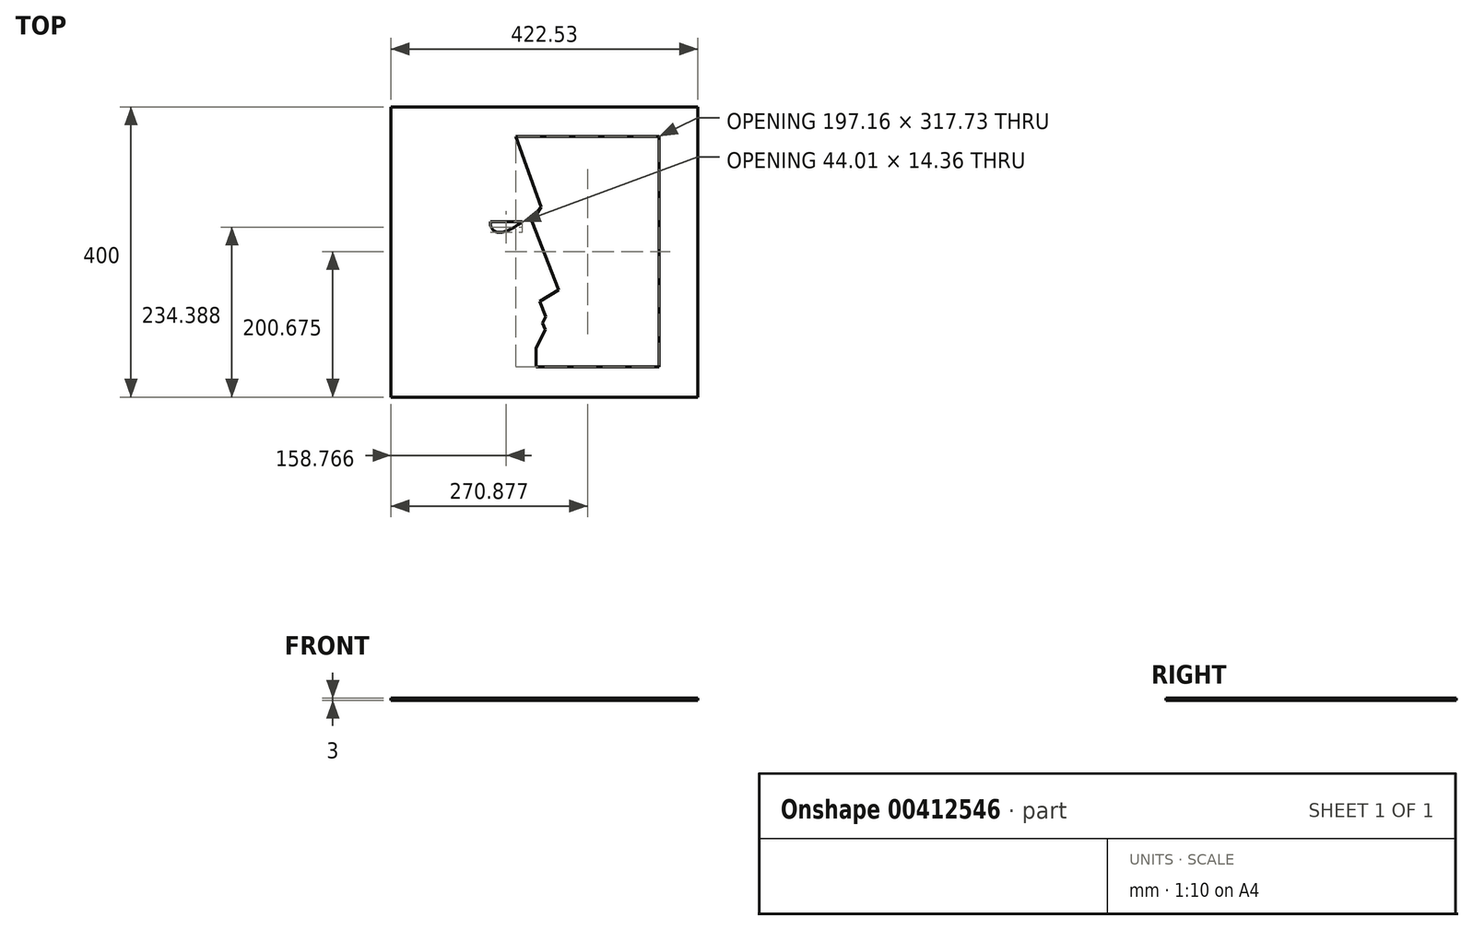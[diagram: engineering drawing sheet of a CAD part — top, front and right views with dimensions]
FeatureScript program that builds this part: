
annotation { "Feature Type Name" : "Feature", "Feature Type Description" : "" }
export const myFeature = defineFeature(function(context is Context, id is Id, definition is map)
    precondition{}
    {
        {
            var Q0;
            Q0=qCreatedBy(makeId("Top.planeOp"),FACE);
            var sketch = newSketch(context, id + "F0", { "sketchPlane" : qUnion([Q0])});
            skLineSegment(sketch, "E0", {"start": v(35.06, -8.57) * mm, "end": v(457.6, -8.57) * mm});
            skLineSegment(sketch, "E1", {"start": v(457.6, -408.57) * mm, "end": v(35.06, -408.57) * mm});
            skLineSegment(sketch, "E2", {"start": v(35.06, -8.57) * mm, "end": v(35.06, -408.57) * mm});
            skLineSegment(sketch, "E3", {"start": v(457.6, -8.57) * mm, "end": v(457.6, -408.57) * mm});
            skLineSegment(sketch, "E4", {"start": v(404.52, -366.76) * mm, "end": v(235.24, -366.76) * mm});
            skLineSegment(sketch, "E5", {"start": v(235.24, -366.76) * mm, "end": v(235.24, -341.4) * mm});
            skLineSegment(sketch, "E6", {"start": v(235.24, -341.4) * mm, "end": v(247.57, -315.1) * mm});
            skLineSegment(sketch, "E7", {"start": v(247.57, -315.1) * mm, "end": v(243.85, -306.66) * mm});
            skLineSegment(sketch, "E8", {"start": v(243.85, -306.66) * mm, "end": v(248.08, -297.64) * mm});
            skLineSegment(sketch, "E9", {"start": v(248.08, -297.64) * mm, "end": v(239.78, -276.47) * mm});
            skLineSegment(sketch, "E10", {"start": v(239.78, -276.47) * mm, "end": v(266.24, -260.85) * mm});
            skLineSegment(sketch, "E11", {"start": v(266.24, -260.85) * mm, "end": v(229, -165.97) * mm});
            skLineSegment(sketch, "E12", {"start": v(229, -165.97) * mm, "end": v(241.68, -146.3) * mm});
            skLineSegment(sketch, "E13", {"start": v(241.68, -146.3) * mm, "end": v(207.36, -49.03) * mm});
            skLineSegment(sketch, "E14", {"start": v(404.52, -366.76) * mm, "end": v(404.52, -49.03) * mm});
            skLineSegment(sketch, "E15", {"start": v(404.52, -49.03) * mm, "end": v(207.36, -49.03) * mm});
            skLineSegment(sketch, "E16", {"start": v(215.83, -167) * mm, "end": v(171.82, -167) * mm});
            skFitSpline(sketch, "E17", {"points": [v(171.82, -167) * mm, v(182.99, -181.36) * mm, v(215.83, -167) * mm], "startDerivative": vector(-1.41, -64.5) * mm, "endDerivative": vector(63.4, 45.28) * mm});
            skSolve(sketch);
        }
        {
            var Q0;
            Q0 = qSketchRegion(id + "F0", true);
            extrude(context, id + "F1", {"entities" : qUnion([Q0]), "depth" : 3 * mm});
        }
    });
